# Revit family: 2069258 Sylvania Lighting Fixture OFFICELYTE 600 HO 4K EM
name_source: partatom
category: Lighting Fixtures
revit_build: Autodesk Revit 2017 (Build: 20190507_1515(x64)
units: mm (PartAtom-declared; Revit-internal decimal feet)

## family parameters
Cut with Voids When Loaded = No
Host = Face
Light Source = Yes
OmniClass Number = 23.80.70.11.17
OmniClass Title = Specialized Lighting by Location or Use
Part Type = Normal
Room Calculation Point = No
Round Connector Dimension = Use Diameter
Shared = No

## types (2) — shared parameters
Assembly Code = D5020200
AssetType = Fixed
Color Filter = 16777215
Description = The Concord OFFICELYTE LP LED HO 4K 600 is a high efficient luminaire for Office, education, meeting rooms. With efficacy of 95lm/W, at 4549lm, CRI of 85 and a very low glare ratio according to EN12464.
Dimming Lamp Color Temperature Shift = <None>
DimmingControlOptions = Non dimmable
DocumentationLiterature = http://www.sylvania-lighting.com
DurationUnit = hours
ElectricShockClassification = Class I
Emit Shape Visible in Rendering = No
Emit from Rectangle Length = 564 mm
Emit from Rectangle Width = 564 mm
ExpectedLife = 50000
Height_SYL = 84 mm
IfcExportAs = IfcLightFixtureType
IfcExportType = IfcLightFixtureType
ImpactProtectionIndex = IK02
IngressProtection = IP20
InputNominalFrequency = 50/60 Hz
InputVoltage = 230-240V~
Keynote = 16500
Lamp = LED
LampColourRenderingIndex = 80
LampColourTemperature = 4000 K
LampNominalLuminous = 4570 lm
LampsType = LED
Length_SYL = 595 mm  [stored 1.9521 ft]
LightOutputRatio = 100
LuminousEfficacy = 131 lm/W
Manufacturer = Havells-Sylvania Group
ManufacturerName = Feilo Sylvania
Material = zintec housing, acrylic diffuser
Material_1_SYL = Steel_Sylvania_Officelyte LP LED_White_RAL 9016
Material_2_SYL = Acrylic_Sylvania_Officelyte LP LED_Satin_4000K
Material_3_SYL = Steel_Sylvania_Officelyte LP LED_White_RAL 9016
ModelNumber = 2069258
NominalHeight = 87 mm
NominalLength = 595 mm  [stored 1.9521 ft]
PowerConsumption = 35 W
PowerFactor = 0.95
Tilt Angle = -90.00°
URL = http://www.sylvania-lighting.com
Voltage = 230 V
Weight = 7.1 kg
Width_SYL = 595 mm  [stored 1.9521 ft]
zero-valued in all types: Default Elevation, NominalWidth

## per-type parameters (varying)
| type | Apparent Load | Model | ModelReference | Name | Photometric Web File | TypeName |
| 2069258 OFFICELYTE 600 HO 4K EM Emergency mode | 2 VA | OFFICELYTE 600 HO 4K EM Emergency mode | OFFICELYTE 600 HO 4K EM Emergency mode | OFFICELYTE 600 HO 4K EM Emergency mode | 2069258EM.ies | OFFICELYTE 600 HO 4K EM Emergency mode |
| 2069258 OFFICELYTE 600 HO 4K EM | 35 VA | OFFICELYTE 600 HO 4K EM | OFFICELYTE 600 HO 4K EM | OFFICELYTE 600 HO 4K EM | 2069258.ies | OFFICELYTE 600 HO 4K EM |

note: [stored X ft] marks values corroborated as IEEE doubles in the binary element streams (Revit-internal decimal feet)

## geometry (parser evidence)
native form markers: Sweep x3
no freeform markers — native parametric forms only
